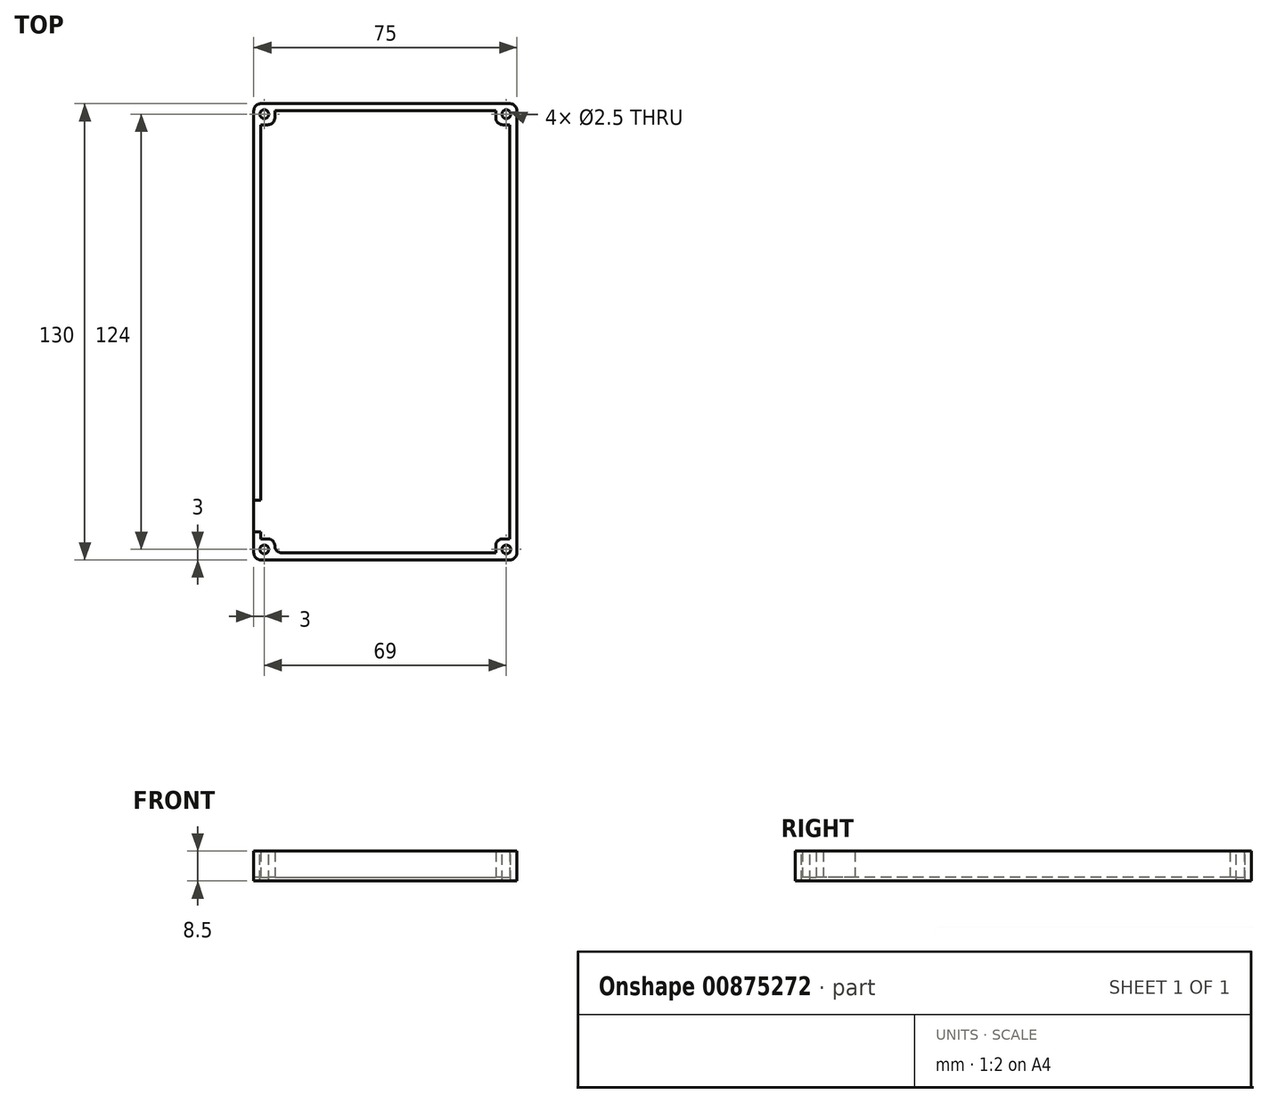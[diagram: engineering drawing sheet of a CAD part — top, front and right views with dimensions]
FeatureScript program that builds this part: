
annotation { "Feature Type Name" : "Feature", "Feature Type Description" : "" }
export const myFeature = defineFeature(function(context is Context, id is Id, definition is map)
    precondition{}
    {
        {
            var Q0;
            Q0=qCreatedBy(makeId("Top.planeOp"),FACE);
            var sketch = newSketch(context, id + "F0", { "sketchPlane" : qUnion([Q0])});
            skLineSegment(sketch, "E0.bottom", {"start": v(-35.5, 59) * mm, "end": v(-31.5, 59) * mm});
            skLineSegment(sketch, "E0.top", {"start": v(-35.5, -59) * mm, "end": v(-31.5, -59) * mm});
            skLineSegment(sketch, "E0.left", {"start": v(-35.5, 59) * mm, "end": v(-35.5, -59) * mm});
            skLineSegment(sketch, "E0.right", {"start": v(35.5, 59) * mm, "end": v(35.5, -59) * mm});
            skPoint(sketch, "E0.middle", {"position": v(0, 0) * mm});
            skLineSegment(sketch, "E1.bottom", {"start": v(-37.5, 65) * mm, "end": v(37.5, 65) * mm});
            skLineSegment(sketch, "E1.top", {"start": v(-37.5, -65) * mm, "end": v(37.5, -65) * mm});
            skLineSegment(sketch, "E1.left", {"start": v(-37.5, 65) * mm, "end": v(-37.5, -65) * mm});
            skLineSegment(sketch, "E1.right", {"start": v(37.5, 65) * mm, "end": v(37.5, -65) * mm});
            skLineSegment(sketch, "E2", {"start": v(-35.5, -57) * mm, "end": v(-37.5, -57) * mm});
            skLineSegment(sketch, "E3", {"start": v(-35.5, -48) * mm, "end": v(-37.5, -48) * mm});
            skLineSegment(sketch, "E4", {"start": v(37.5, -62) * mm, "end": v(-37.5, -62) * mm, "construction": true});
            skCircle(sketch, "E5", {"center": v(-34.5, -62) * mm, "radius": 1.25 * mm});
            skCircle(sketch, "E6", {"center": v(34.5, -62) * mm, "radius": 1.25 * mm});
            skLineSegment(sketch, "E7.top", {"start": v(-31.5, -63) * mm, "end": v(31.5, -63) * mm});
            skLineSegment(sketch, "E7.left", {"start": v(-31.5, -59) * mm, "end": v(-31.5, -63) * mm});
            skLineSegment(sketch, "E7.right", {"start": v(31.5, -59) * mm, "end": v(31.5, -63) * mm});
            skLineSegment(sketch, "E8.trimOffspring", {"start": v(31.5, -59) * mm, "end": v(35.5, -59) * mm});
            skLineSegment(sketch, "E9", {"start": v(37.5, 62) * mm, "end": v(-37.5, 62) * mm, "construction": true});
            skCircle(sketch, "E10", {"center": v(-34.5, 62) * mm, "radius": 1.25 * mm});
            skCircle(sketch, "E11", {"center": v(34.5, 62) * mm, "radius": 1.25 * mm});
            skLineSegment(sketch, "E12.top", {"start": v(-31.5, 63) * mm, "end": v(31.5, 63) * mm});
            skLineSegment(sketch, "E12.left", {"start": v(-31.5, 59) * mm, "end": v(-31.5, 63) * mm});
            skLineSegment(sketch, "E12.right", {"start": v(31.5, 59) * mm, "end": v(31.5, 63) * mm});
            skLineSegment(sketch, "E13.trimOffspring", {"start": v(31.5, 59) * mm, "end": v(35.5, 59) * mm});
            skSolve(sketch);
        }
        {
            var Q0;
            {var subQ4=sQuery(id+"F0.wireOp",EDGE,"E0.bottom");Q0=makeQuery(id+"F0.imprint","IMPRINT",FACE,{"disambiguationData":[TD([[makeQuery(id+"F0.imprint","IMPRINT",EDGE,{"derivedFrom":subQ4}),1.0]])]});}
            var Q1;
            {var subQ3=sQuery(id+"F0.wireOp",EDGE,"E0.bottom");Q1=makeQuery(id+"F0.imprint","IMPRINT",FACE,{"disambiguationData":[TD([[makeQuery(id+"F0.imprint","IMPRINT",EDGE,{"derivedFrom":subQ3}),-1.0]])]});}
            var Q2;
            {var subQ0=sQuery(id+"F0.wireOp",EDGE,"E2");Q2=makeQuery(id+"F0.imprint","IMPRINT",FACE,{"disambiguationData":[TD([[makeQuery(id+"F0.imprint","IMPRINT",EDGE,{"derivedFrom":subQ0}),-1.0]])]});}
            extrude(context, id + "F1", {"entities" : qUnion([Q0, Q1, Q2]), "depth" : -1 * mm, "offsetDistance" : 25 * mm});
        }
        {
            var Q0;
            {var subQ4=sQuery(id+"F0.wireOp",EDGE,"E0.bottom");Q0=makeQuery(id+"F0.imprint","IMPRINT",FACE,{"disambiguationData":[TD([[makeQuery(id+"F0.imprint","IMPRINT",EDGE,{"derivedFrom":subQ4}),1.0]])]});}
            extrude(context, id + "F2", {"entities" : qUnion([Q0]), "operationType" : NewBodyOperationType.ADD, "depth" : 7.5 * mm, "offsetDistance" : 25 * mm});
        }
        {
            var Q0;
            {var subQ0=sQuery(id+"F0.wireOp",EDGE,"E1.right");var subQ1=sQuery(id+"F0.wireOp",EDGE,"E1.top");Q0=makeQuery(id+"F2.boolean.opBoolean","MERGE",EDGE,{"derivedFrom":[makeQuery(id+"F1.opExtrude","SWEPT_EDGE",EDGE,{"disambiguationData":[OSD([subQ1,subQ0])]}),makeQuery(id+"F2.opExtrude","SWEPT_EDGE",EDGE,{"disambiguationData":[OSD([subQ1,subQ0])]})]});}
            var Q1;
            {var subQ0=sQuery(id+"F0.wireOp",EDGE,"E1.right");var subQ1=sQuery(id+"F0.wireOp",EDGE,"E1.bottom");Q1=makeQuery(id+"F2.boolean.opBoolean","MERGE",EDGE,{"derivedFrom":[makeQuery(id+"F1.opExtrude","SWEPT_EDGE",EDGE,{"disambiguationData":[OSD([subQ1,subQ0])]}),makeQuery(id+"F2.opExtrude","SWEPT_EDGE",EDGE,{"disambiguationData":[OSD([subQ1,subQ0])]})]});}
            var Q2;
            {var subQ0=sQuery(id+"F0.wireOp",EDGE,"E1.left");var subQ1=sQuery(id+"F0.wireOp",EDGE,"E1.bottom");Q2=makeQuery(id+"F2.boolean.opBoolean","MERGE",EDGE,{"derivedFrom":[makeQuery(id+"F1.opExtrude","SWEPT_EDGE",EDGE,{"disambiguationData":[OSD([subQ1,subQ0])]}),makeQuery(id+"F2.opExtrude","SWEPT_EDGE",EDGE,{"disambiguationData":[OSD([subQ1,subQ0])]})]});}
            var Q3;
            Q3=makeQuery(id+"F2.opExtrude","SWEPT_EDGE",EDGE,{"disambiguationData":[OSD([sQuery(id+"F0.wireOp",EDGE,"E7.right"),sQuery(id+"F0.wireOp",EDGE,"E8.trimOffspring")])]});
            var Q4;
            Q4=makeQuery(id+"F2.opExtrude","SWEPT_EDGE",EDGE,{"disambiguationData":[OSD([sQuery(id+"F0.wireOp",EDGE,"E7.top"),sQuery(id+"F0.wireOp",EDGE,"E7.left")])]});
            var Q5;
            {var subQ0=sQuery(id+"F0.wireOp",EDGE,"E1.left");var subQ1=sQuery(id+"F0.wireOp",EDGE,"E1.top");Q5=makeQuery(id+"F2.boolean.opBoolean","MERGE",EDGE,{"derivedFrom":[makeQuery(id+"F1.opExtrude","SWEPT_EDGE",EDGE,{"disambiguationData":[OSD([subQ1,subQ0])]}),makeQuery(id+"F2.opExtrude","SWEPT_EDGE",EDGE,{"disambiguationData":[OSD([subQ1,subQ0])]})]});}
            var Q6;
            Q6=makeQuery(id+"F2.opExtrude","SWEPT_EDGE",EDGE,{"disambiguationData":[OSD([sQuery(id+"F0.wireOp",EDGE,"E0.bottom"),sQuery(id+"F0.wireOp",EDGE,"E12.left")])]});
            var Q7;
            Q7=makeQuery(id+"F2.opExtrude","SWEPT_EDGE",EDGE,{"disambiguationData":[OSD([sQuery(id+"F0.wireOp",EDGE,"E12.right"),sQuery(id+"F0.wireOp",EDGE,"E13.trimOffspring")])]});
            var Q8;
            Q8=makeQuery(id+"F2.opExtrude","SWEPT_EDGE",EDGE,{"disambiguationData":[OSD([sQuery(id+"F0.wireOp",EDGE,"E0.top"),sQuery(id+"F0.wireOp",EDGE,"E7.left")])]});
            fillet(context, id + "F3", {"entities" : qUnion([Q0, Q1, Q2, Q3, Q4, Q5, Q6, Q7, Q8]), "tangentPropagation" : true, "radius" : 2 * mm, "defaultsChanged" : false, "vertexSettings" : [], "allowEdgeOverflow" : false});
        }
    });
